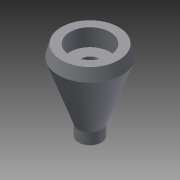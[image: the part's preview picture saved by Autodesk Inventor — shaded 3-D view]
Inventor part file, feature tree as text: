
AUTODESK INVENTOR PART (.ipt)
format: ipt  version: 2015 (Build 190159000, 159)  size: 102,912 bytes
history: native  units: in
note: dims shown in document units (in); Inventor stores cm internally (conversion verified against a paired STEP export)
features: sketch x2, revolve x1, hole x1, chamfer x1
ambient origin geometry x8: Origin, YZ Plane, XZ Plane, XY Plane, X Axis, Y Axis, Z Axis, Center Point
bodies: Solid1 (feature_tree)
feature tree (5):
  revolve  "Revolution1"  [1 undecoded]
  hole  "Hole1"  [1 undecoded]
  chamfer  "Chamfer1"  Distance=1.5in
  sketch  "Sketch1"  dims[d0=0.25in d1=0.25in]
  sketch  "Sketch2"  dims[d2=1.75in d3=75.0deg d4=1.5in d5=90.0deg d6=0.375in d7=0.75in d8=0.875in d9=0.375in d10=0.5635in d11=1.5in d12=0.8108in d13=0.01in d14=0.125in d15=45.0deg]
note: 2 required parameter values undecoded (feature->parameter linkage not recoverable at this tier; creation-order binding heuristic only, values carry confidence <= 0.55)